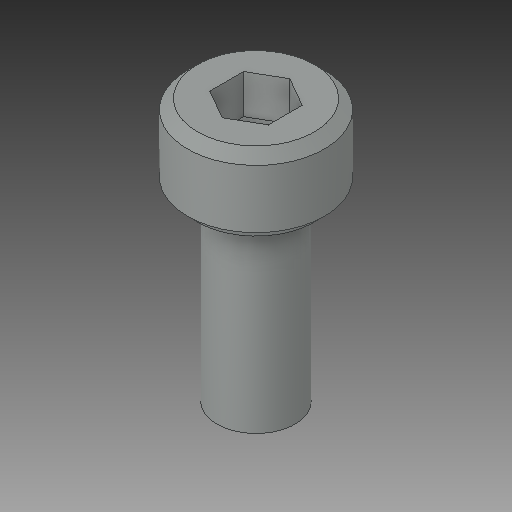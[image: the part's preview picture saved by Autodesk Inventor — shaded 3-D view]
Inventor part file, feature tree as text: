
AUTODESK INVENTOR PART (.ipt)
format: ipt  version: 2019 (Build 230136000, 136)  size: 106,496 bytes
history: native  units: in
note: dims shown in document units (in); Inventor stores cm internally (conversion verified against a paired STEP export)
features: chamfer x1
ambient origin geometry x8: Origin, YZ Plane, XZ Plane, XY Plane, X Axis, Y Axis, Z Axis, Center Point
bodies: Solid1 (feature_tree)
feature tree (1):
  chamfer  "Chamfer2"  [1 undecoded]
note: 1 required parameter value undecoded (feature->parameter linkage not recoverable at this tier; creation-order binding heuristic only, values carry confidence <= 0.55)
